# Revit family: IS_ConnectAir_E1147_BIM_FR
name_source: partatom
category: Plumbing Fixtures
revit_build: Autodesk Revit 2017 (Build: 20160225_1515(x64)
units: mm (PartAtom-declared; Revit-internal decimal feet)

## family parameters
Cut with Voids When Loaded = No
Host = Face
OmniClass Number = 23.45.05.14.17.11
OmniClass Title = Shower Compartments
Part Type = Normal
Room Calculation Point = No
Round Connector Dimension = Use Diameter
Shared = Yes

## types (5) — shared parameters
Accessoires = www.idealstandard.be
Assembly Code = C1030200
Bim-NomDuProjet = ISI_IdealStandard_ConnectAir_E1147
ConseilsDInstallation = www.idealstandard.be
DateDeCréation = 2018_08_15
Default Elevation = 800 mm  [stored 2.62467 ft]
Dimensions = 18 x 1300 x 440 mm
Espace = Interne
Forme = Complexe
Hauteur = 18 mm  [stored 0.0590551 ft]
IfcExportAs = IfcFurnitureType
IfcExportType = USERDEFINED
InformationsProduit = www.idealstandard.be
Largeur = 1300 mm  [stored 4.26509 ft]
LienUtile = www.idealstandard.be
Longueur = 440 mm  [stored 1.44357 ft]
Manufacturer = www.idealstandard.be
Marque = Ideal Standard
Matériel = Panneau de fibres
NBSDescription = Bathroom cabinets
NBSReference = 45-35-72/320
Raccordement = Plomberie
Révision = 1
URL = www.idealstandard.be
Uniclass2015Code = Pr_40_30_78_05
Uniclass2015Title = Bathroom integrated furniture
UnitéDeMesure = Millimètres
UnitéDeTemps = An
UnitéMonétaire = €
UrlDuFabricant = www.idealstandard.be
zero-valued in all types: CWFU, Cost, CoûtDeRemplacement, HWFU, Profondeur, WFU

## per-type parameters (varying)
| type | Caractéristiques | Couleur | Description | Finition | MainColour | Model | PoidsNet |
| E1147B2 - 130CM Worktop for Vessel Installation Gls Matt White | -2146826246 | 0 | -2146826246 | 0 | ISI_IdealStandard_Laminate_White_Render | E1142B2 |  |
| E1147PS - 130CM Worktop for Vessel Installation Gls Light Grey | Plan Pour Installation Vasque | Wood Light Grey+Mat Blanc | Plan Pour Installation Vasque | Wood Light Grey+Mat Blanc | ISI_IdealStandard_Furniture_Grey_Render | E1147PS | 9 Kg |
| E1147EQ - 130CM Worktop for Vessel Installation Wood Light Grey | Plan Pour Installation Vasque | Brilliant Light Grey+Mat Blanc | Plan Pour Installation Vasque | Brilliant Light Grey+Mat Blanc | ISI_IdealStandard_Furniture_WoodLightGrey_Render | E1147EQ | 9 Kg |
| E1147UK - 130CM Worktop for Vessel Installation Wood Light Brown | Plan Pour Installation Vasque | Wood Light Brown+Mat Lt Brown | Plan Pour Installation Vasque | Wood Light Brown+Mat Lt Brown | ISI_IdealStandard__WoodLightBrown_Render | E1147UK | 9 Kg |
| E1147VY - 130CM Worktop for Vessel Installation Matt Dark Brown | Plan Pour Installation Vasque | Mat Dark Brown+Mat Blanc | Plan Pour Installation Vasque | Mat Dark Brown+Mat Blanc | ISI_IdealStandard_Furniture_DarkBrown_Render | E1147VY | 9 Kg |

note: [stored X ft] marks values corroborated as IEEE doubles in the binary element streams (Revit-internal decimal feet)

## geometry (parser evidence)
native form markers: Sweep x3
no freeform markers — native parametric forms only
